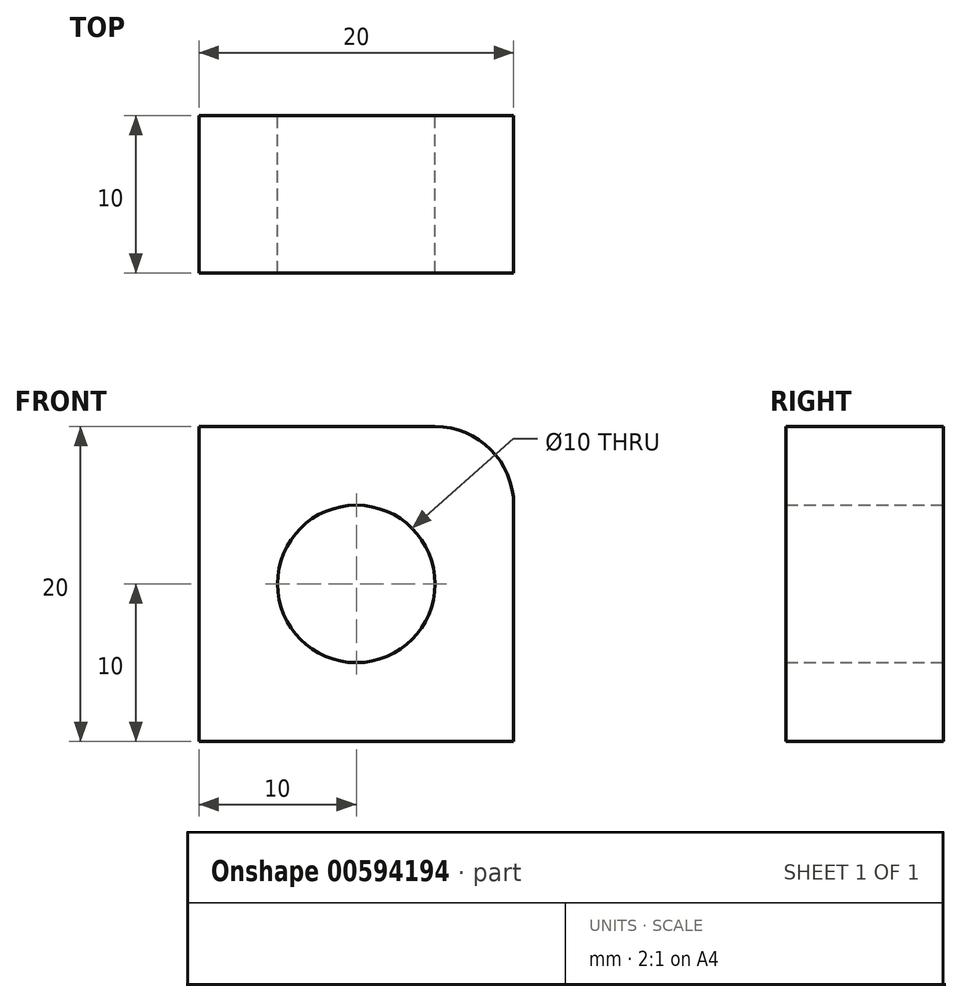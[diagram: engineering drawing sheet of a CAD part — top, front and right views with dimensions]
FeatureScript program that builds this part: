
annotation { "Feature Type Name" : "Feature", "Feature Type Description" : "" }
export const myFeature = defineFeature(function(context is Context, id is Id, definition is map)
    precondition{}
    {
        {
            var Q0;
            Q0=qCreatedBy(makeId("Front.planeOp"),FACE);
            var sketch = newSketch(context, id + "F0", { "sketchPlane" : qUnion([Q0])});
            skLineSegment(sketch, "E0.bottom", {"start": v(10, -10) * mm, "end": v(-10, -10) * mm});
            skLineSegment(sketch, "E0.top", {"start": v(5, 10) * mm, "end": v(-10, 10) * mm});
            skLineSegment(sketch, "E0.left", {"start": v(10, -10) * mm, "end": v(10, 5) * mm});
            skLineSegment(sketch, "E0.right", {"start": v(-10, -10) * mm, "end": v(-10, 10) * mm});
            skPoint(sketch, "E0.middle", {"position": v(0, 0) * mm});
            skPoint(sketch, "E1.visualSharp", {"position": v(10, 10) * mm});
            skArc(sketch, "E1.filletArc", {"start": v(10, 5) * mm, "mid": v(8.54, 8.54) * mm, "end": v(5, 10) * mm});
            skCircle(sketch, "E2", {"center": v(0, 0) * mm, "radius": 5 * mm});
            skSolve(sketch);
        }
        {
            var Q0;
            Q0=makeQuery(id+"F0.imprint","IMPRINT",FACE,{"disambiguationData":[TD([[makeQuery(id+"F0.imprint","IMPRINT",EDGE,{"derivedFrom":sQuery(id+"F0.wireOp",EDGE,"E0.bottom")}),-1.0]])]});
            extrude(context, id + "F1", {"entities" : qUnion([Q0]), "depth" : 10 * mm, "offsetDistance" : 25 * mm});
        }
    });
